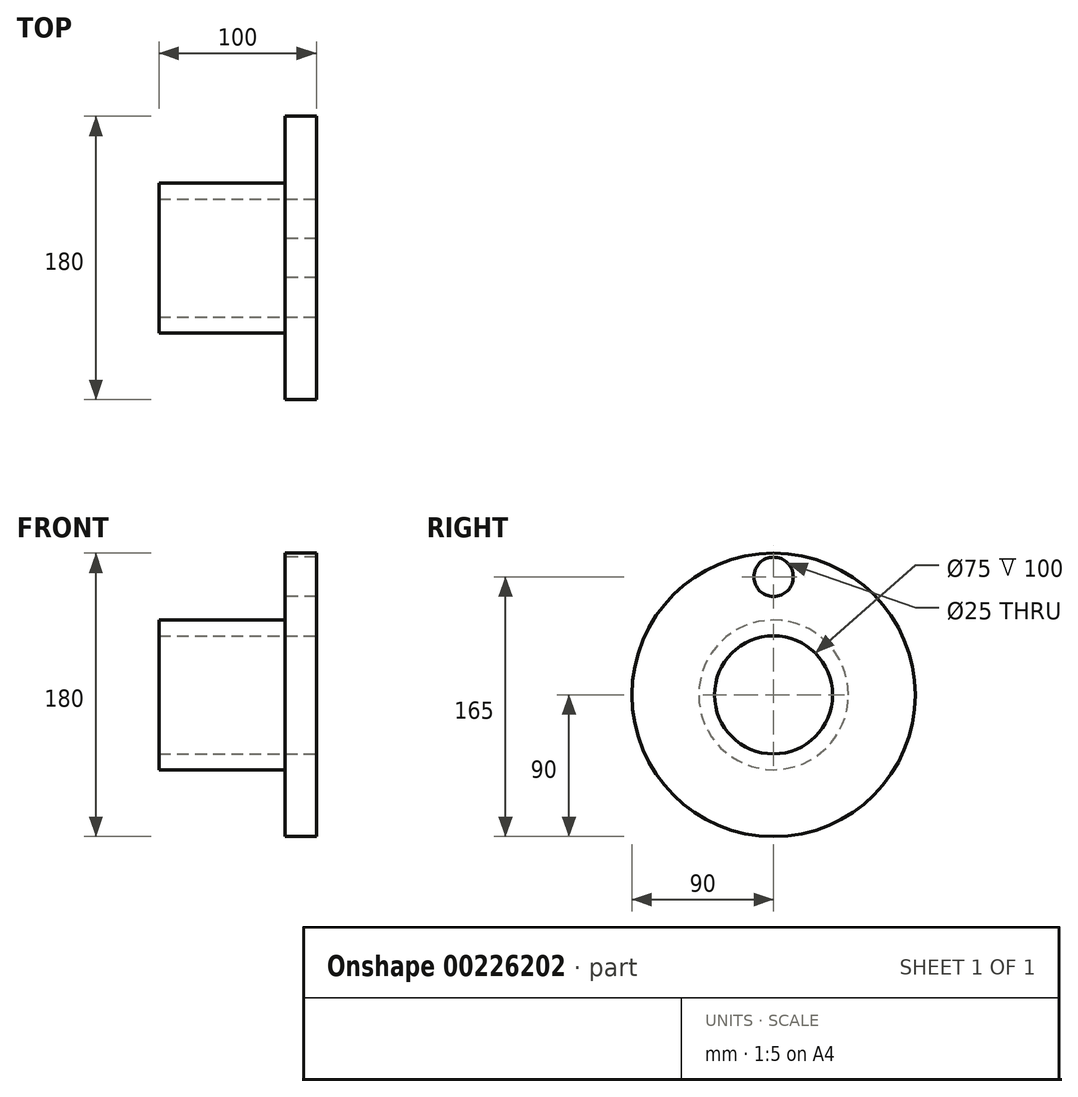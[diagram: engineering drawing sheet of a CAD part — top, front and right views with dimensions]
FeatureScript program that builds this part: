
annotation { "Feature Type Name" : "Feature", "Feature Type Description" : "" }
export const myFeature = defineFeature(function(context is Context, id is Id, definition is map)
    precondition{}
    {
        {
            var Q0;
            Q0=qCreatedBy(makeId("Front.planeOp"),FACE);
            var sketch = newSketch(context, id + "F0", { "sketchPlane" : qUnion([Q0])});
            skLineSegment(sketch, "E0", {"start": v(0, 0) * mm, "end": v(-116.98, 0) * mm, "construction": true});
            skLineSegment(sketch, "E1.bottom", {"start": v(0, 37.5) * mm, "end": v(-100, 37.5) * mm});
            skLineSegment(sketch, "E1.top", {"start": v(0, 90) * mm, "end": v(-20, 90) * mm});
            skLineSegment(sketch, "E1.left", {"start": v(0, 37.5) * mm, "end": v(0, 90) * mm});
            skLineSegment(sketch, "E1.right", {"start": v(-100, 37.5) * mm, "end": v(-100, 47.5) * mm});
            skLineSegment(sketch, "E2.top", {"start": v(-100, 47.5) * mm, "end": v(-20, 47.5) * mm});
            skLineSegment(sketch, "E2.right", {"start": v(-20, 90) * mm, "end": v(-20, 47.5) * mm});
            skSolve(sketch);
        }
        {
            var Q0;
            Q0 = qSketchRegion(id + "F0", true);
            var Q1;
            Q1=sQuery(id+"F0.wireOp",EDGE,"E0");
            revolve(context, id + "F1", {"entities" : qUnion([Q0]), "axis" : qUnion([Q1]), "revolveType" : RevolveType.FULL});
        }
        {
            var Q0;
            Q0=makeQuery(id+"F1.opRevolve","SWEPT_FACE",FACE,{"disambiguationData":[OSD([sQuery(id+"F0.wireOp",EDGE,"E2.right")])]});
            var sketch = newSketch(context, id + "F2", { "sketchPlane" : qUnion([Q0])});
            skCircle(sketch, "E3", {"center": v(0, 75) * mm, "radius": 12.5 * mm});
            skSolve(sketch);
        }
        {
            var Q0;
            Q0=makeQuery(id+"F2.imprint","IMPRINT",FACE,{"disambiguationData":[TD([[makeQuery(id+"F2.imprint","IMPRINT",EDGE,{"derivedFrom":sQuery(id+"F2.wireOp",EDGE,"E3")}),1.0]])]});
            extrude(context, id + "F3", {"entities" : qUnion([Q0]), "operationType" : NewBodyOperationType.REMOVE, "oppositeDirection" : true, "depth" : 25 * mm});
        }
    });
